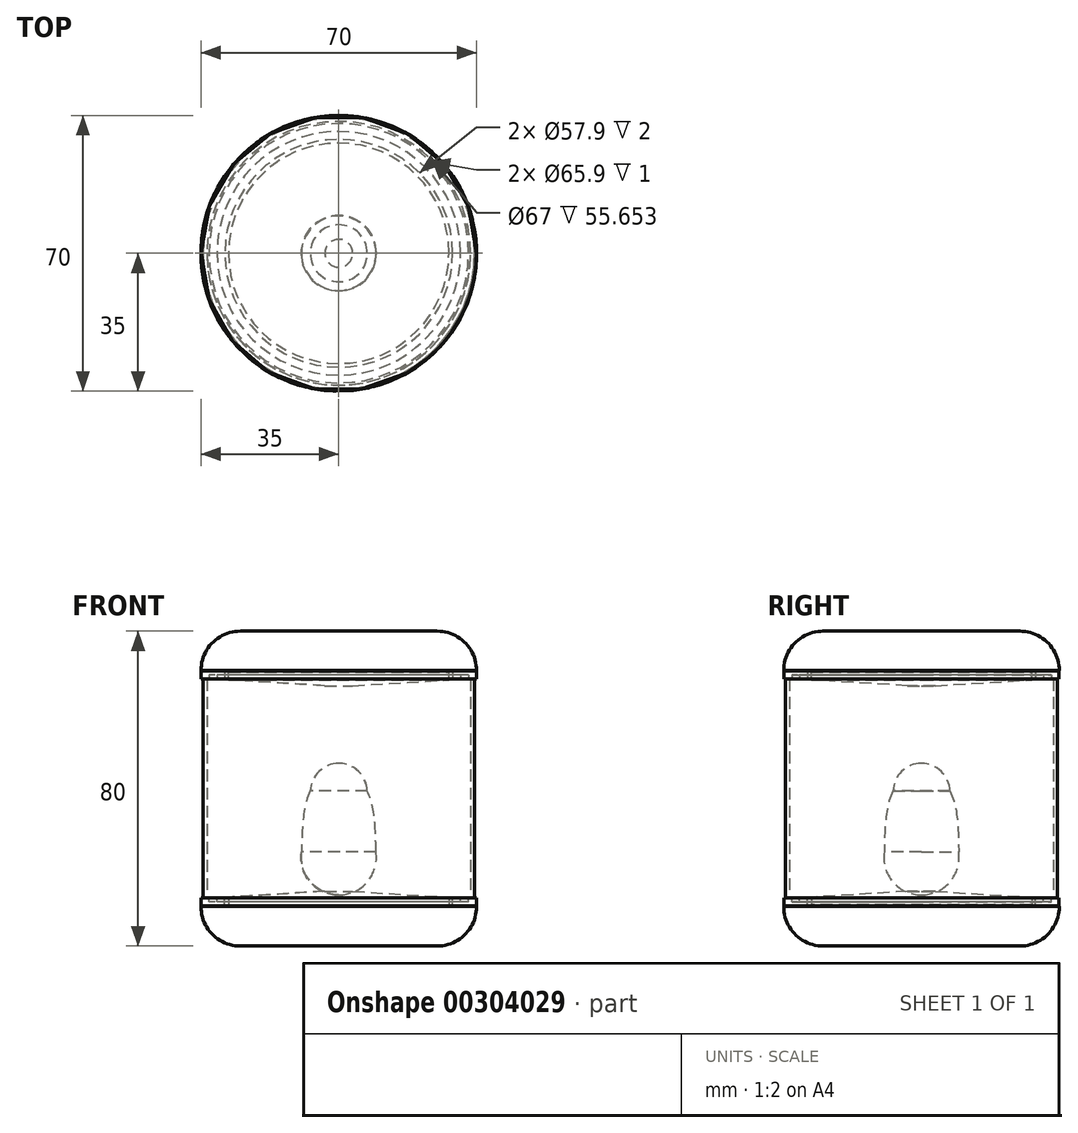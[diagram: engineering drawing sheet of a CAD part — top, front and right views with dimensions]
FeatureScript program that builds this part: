
annotation { "Feature Type Name" : "Feature", "Feature Type Description" : "" }
export const myFeature = defineFeature(function(context is Context, id is Id, definition is map)
    precondition{}
    {
        {
            var Q0;
            Q0=qCreatedBy(makeId("Front.planeOp"),FACE);
            var sketch = newSketch(context, id + "F0", { "sketchPlane" : qUnion([Q0])});
            skLineSegment(sketch, "E0", {"start": v(0, 0) * mm, "end": v(-25, 0) * mm});
            skLineSegment(sketch, "E1", {"start": v(-21.06, 10.03) * mm, "end": v(0, 10.03) * mm});
            skLineSegment(sketch, "E2", {"start": v(0, 10.03) * mm, "end": v(0, 0) * mm});
            skArc(sketch, "E3", {"start": v(-25, 0) * mm, "mid": v(-32.08, 2.94) * mm, "end": v(-35, 10.03) * mm});
            skLineSegment(sketch, "E4", {"start": v(-35, 10.03) * mm, "end": v(-21.06, 10.03) * mm});
            skSolve(sketch);
        }
        {
            var Q0;
            Q0 = qSketchRegion(id + "F0", true);
            var Q1;
            Q1=sQuery(id+"F0.wireOp",EDGE,"E2");
            revolve(context, id + "F1", {"entities" : qUnion([Q0]), "axis" : qUnion([Q1]), "revolveType" : RevolveType.FULL});
        }
        {
            var Q0;
            Q0=qCreatedBy(makeId("Front.planeOp"),FACE);
            var sketch = newSketch(context, id + "F2", { "sketchPlane" : qUnion([Q0])});
            skLineSegment(sketch, "E5", {"start": v(-34.95, 10.17) * mm, "end": v(-28.95, 10.17) * mm});
            skLineSegment(sketch, "E6", {"start": v(-28.95, 10.17) * mm, "end": v(-28.95, 12.17) * mm});
            skLineSegment(sketch, "E7", {"start": v(-28.95, 12.17) * mm, "end": v(-30.95, 12.17) * mm});
            skLineSegment(sketch, "E8", {"start": v(-30.95, 12.17) * mm, "end": v(-30.95, 11.17) * mm});
            skLineSegment(sketch, "E9", {"start": v(-30.95, 11.17) * mm, "end": v(-32.95, 11.17) * mm});
            skLineSegment(sketch, "E10", {"start": v(-32.95, 11.17) * mm, "end": v(-32.95, 12.17) * mm});
            skLineSegment(sketch, "E11", {"start": v(-32.95, 12.17) * mm, "end": v(-34.95, 12.17) * mm});
            skLineSegment(sketch, "E12", {"start": v(-34.95, 12.17) * mm, "end": v(-34.95, 10.17) * mm});
            skLineSegment(sketch, "E13", {"start": v(0, 54.16) * mm, "end": v(0, -8.32) * mm, "construction": true});
            skSolve(sketch);
        }
        {
            var Q0;
            Q0 = qSketchRegion(id + "F2", true);
            var Q1;
            Q1=sQuery(id+"F2.wireOp",EDGE,"E13");
            revolve(context, id + "F3", {"entities" : qUnion([Q0]), "axis" : qUnion([Q1]), "revolveType" : RevolveType.FULL});
        }
        {
            var Q0;
            Q0=qCreatedBy(makeId("Front.planeOp"),FACE);
            var sketch = newSketch(context, id + "F4", { "sketchPlane" : qUnion([Q0])});
            skLineSegment(sketch, "E14", {"start": v(0, 10.39) * mm, "end": v(-28, 10.39) * mm});
            skLineSegment(sketch, "E15", {"start": v(0, 10.39) * mm, "end": v(0, 13.89) * mm});
            skLineSegment(sketch, "E16", {"start": v(-28, 10.39) * mm, "end": v(-28, 12.39) * mm});
            skLineSegment(sketch, "E17", {"start": v(0, 13.89) * mm, "end": v(-3.56, 13.89) * mm});
            skLineSegment(sketch, "E18", {"start": v(-3.56, 13.89) * mm, "end": v(-28, 12.39) * mm});
            skSolve(sketch);
        }
        {
            var Q0;
            Q0 = qSketchRegion(id + "F4", true);
            var Q1;
            Q1=sQuery(id+"F4.wireOp",EDGE,"E15");
            revolve(context, id + "F5", {"entities" : qUnion([Q0]), "axis" : qUnion([Q1]), "revolveType" : RevolveType.FULL});
        }
        {
            var Q0;
            Q0=qCreatedBy(makeId("Front.planeOp"),FACE);
            var sketch = newSketch(context, id + "F6", { "sketchPlane" : qUnion([Q0])});
            skLineSegment(sketch, "E19.bottom", {"start": v(-34.5, 12) * mm, "end": v(-33.5, 12) * mm});
            skLineSegment(sketch, "E19.top", {"start": v(-34.5, 40) * mm, "end": v(-33.5, 40) * mm});
            skLineSegment(sketch, "E19.left", {"start": v(-34.5, 12) * mm, "end": v(-34.5, 40) * mm});
            skLineSegment(sketch, "E19.right", {"start": v(-33.5, 12) * mm, "end": v(-33.5, 40) * mm});
            skLineSegment(sketch, "E20", {"start": v(0, 0) * mm, "end": v(0, 42.17) * mm, "construction": true});
            skLineSegment(sketch, "E21", {"start": v(0, 42.17) * mm, "end": v(0, 60.2) * mm, "construction": true});
            skLineSegment(sketch, "E22", {"start": v(0, 60.2) * mm, "end": v(0, -5.84) * mm, "construction": true});
            skLineSegment(sketch, "E23", {"start": v(0, -5.84) * mm, "end": v(0, 42.17) * mm, "construction": true});
            skSolve(sketch);
        }
        {
            var Q0;
            Q0 = qSketchRegion(id + "F6", true);
            var Q1;
            Q1=sQuery(id+"F6.wireOp",EDGE,"E23");
            revolve(context, id + "F7", {"entities" : qUnion([Q0]), "axis" : qUnion([Q1]), "revolveType" : RevolveType.FULL});
        }
        {
            var Q0;
            Q0=makeQuery(id+"F5.opRevolve","SWEPT_BODY",BODY,{"disambiguationData":[OSD([sQuery(id+"F4.wireOp",EDGE,"E14"),sQuery(id+"F4.wireOp",EDGE,"E15"),sQuery(id+"F4.wireOp",EDGE,"E16"),sQuery(id+"F4.wireOp",EDGE,"E17"),sQuery(id+"F4.wireOp",EDGE,"E18")])]});
            var Q1;
            Q1=makeQuery(id+"F3.opRevolve","SWEPT_BODY",BODY,{"disambiguationData":[OSD([sQuery(id+"F2.wireOp",EDGE,"E5"),sQuery(id+"F2.wireOp",EDGE,"E6"),sQuery(id+"F2.wireOp",EDGE,"E7"),sQuery(id+"F2.wireOp",EDGE,"E8"),sQuery(id+"F2.wireOp",EDGE,"E9"),sQuery(id+"F2.wireOp",EDGE,"E10"),sQuery(id+"F2.wireOp",EDGE,"E11"),sQuery(id+"F2.wireOp",EDGE,"E12")])]});
            var Q2;
            Q2=makeQuery(id+"F1.opRevolve","SWEPT_BODY",BODY,{"disambiguationData":[OSD([sQuery(id+"F0.wireOp",EDGE,"E0"),sQuery(id+"F0.wireOp",EDGE,"E1"),sQuery(id+"F0.wireOp",EDGE,"E2"),sQuery(id+"F0.wireOp",EDGE,"E3"),sQuery(id+"F0.wireOp",EDGE,"E4")])]});
            var Q3;
            Q3=makeQuery(id+"F7.opRevolve","SWEPT_FACE",FACE,{"disambiguationData":[OSD([sQuery(id+"F6.wireOp",EDGE,"E19.top")])]});
            mirror(context, id + "F8", {"entities" : qUnion([Q0, Q1, Q2]), "mirrorPlane" : qUnion([Q3])});
        }
        {
            var Q0;
            Q0=makeQuery(id+"F7.opRevolve","SWEPT_BODY",BODY,{"disambiguationData":[OSD([sQuery(id+"F6.wireOp",EDGE,"E19.bottom"),sQuery(id+"F6.wireOp",EDGE,"E19.top"),sQuery(id+"F6.wireOp",EDGE,"E19.left"),sQuery(id+"F6.wireOp",EDGE,"E19.right")])]});
            var Q1;
            Q1=makeQuery(id+"F7.opRevolve","SWEPT_FACE",FACE,{"disambiguationData":[OSD([sQuery(id+"F6.wireOp",EDGE,"E19.top")])]});
            mirror(context, id + "F9", {"operationType" : NewBodyOperationType.ADD, "entities" : qUnion([Q0]), "mirrorPlane" : qUnion([Q1])});
        }
        {
            var Q0;
            Q0=qCreatedBy(makeId("Front.planeOp"),FACE);
            var sketch = newSketch(context, id + "F10", { "sketchPlane" : qUnion([Q0])});
            skArc(sketch, "E24.trimOffspring", {"start": v(-9.47, 23.9) * mm, "mid": v(-7.23, 16.26) * mm, "end": v(0, 12.96) * mm});
            skLineSegment(sketch, "E25", {"start": v(0, 46.39) * mm, "end": v(0, 12.96) * mm});
            skArc(sketch, "E26.trimOffspring", {"start": v(0, 46.39) * mm, "mid": v(-5.04, 44.34) * mm, "end": v(-7.24, 39.36) * mm});
            skPoint(sketch, "E27.end.orphan", {"position": v(7, 41) * mm});
            skPoint(sketch, "E28.orphan", {"position": v(9.47, 23.9) * mm});
            skFitSpline(sketch, "E29", {"points": [v(-9.47, 23.9) * mm, v(-7.24, 39.36) * mm, v(0, 46.39) * mm], "startDerivative": vector(0.64, 31.25) * mm, "endDerivative": vector(18.96, 13.08) * mm});
            skSolve(sketch);
        }
        {
            var Q0;
            Q0 = qSketchRegion(id + "F10", true);
            var Q1;
            Q1=sQuery(id+"F10.wireOp",EDGE,"E25");
            revolve(context, id + "F11", {"entities" : qUnion([Q0]), "axis" : qUnion([Q1]), "revolveType" : RevolveType.FULL});
        }
    });
